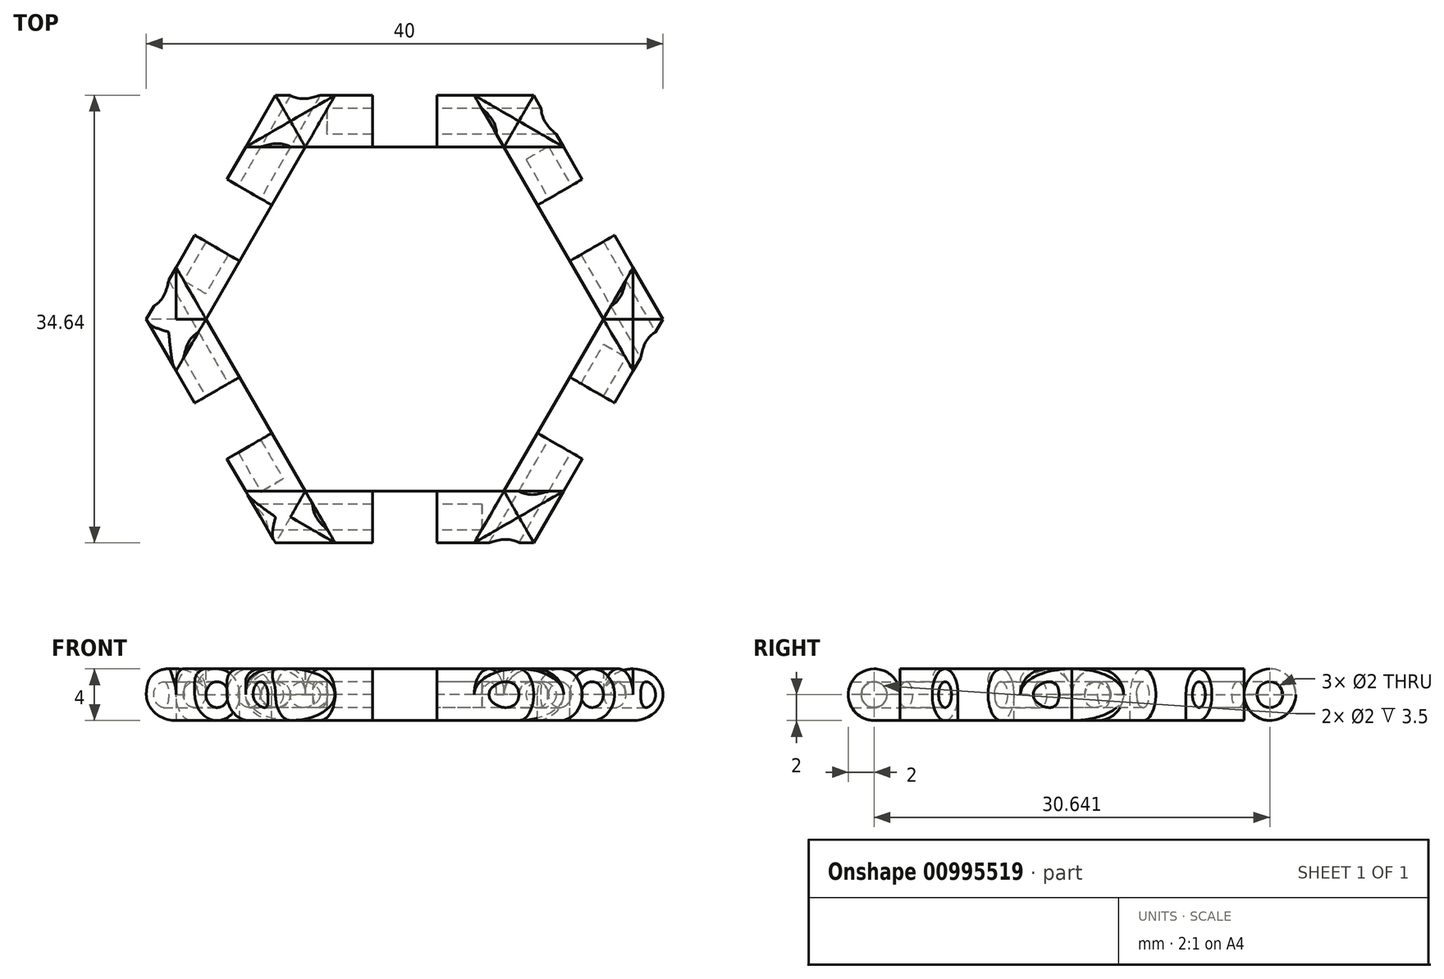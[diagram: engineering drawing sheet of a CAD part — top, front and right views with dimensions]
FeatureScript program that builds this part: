
annotation { "Feature Type Name" : "Feature", "Feature Type Description" : "" }
export const myFeature = defineFeature(function(context is Context, id is Id, definition is map)
    precondition{}
    {
        {
            var Q0;
            Q0=qCreatedBy(makeId("Top.planeOp"),FACE);
            var sketch = newSketch(context, id + "F0", { "sketchPlane" : qUnion([Q0])});
            skPoint(sketch, "E0.center", {"position": v(0, 0) * mm});
            skLineSegment(sketch, "E1", {"start": v(-10, -17.32) * mm, "end": v(10, -17.32) * mm});
            skLineSegment(sketch, "E2", {"start": v(10, -17.32) * mm, "end": v(20, 0) * mm});
            skLineSegment(sketch, "E3", {"start": v(20, 0) * mm, "end": v(10, 17.32) * mm});
            skLineSegment(sketch, "E4", {"start": v(10, 17.32) * mm, "end": v(-10, 17.32) * mm});
            skLineSegment(sketch, "E5", {"start": v(-10, 17.32) * mm, "end": v(-20, 0) * mm});
            skLineSegment(sketch, "E6", {"start": v(-20, 0) * mm, "end": v(-10, -17.32) * mm});
            skSolve(sketch);
        }
        {
            var Q0;
            Q0=makeQuery(id+"F0.imprint","IMPRINT",FACE,{"disambiguationData":[TD([[makeQuery(id+"F0.imprint","IMPRINT",EDGE,{"derivedFrom":sQuery(id+"F0.wireOp",EDGE,"E1")}),1.0]])]});
            extrude(context, id + "F1", {"entities" : qUnion([Q0]), "depth" : 4 * mm, "offsetDistance" : 25 * mm});
        }
        {
            var Q0;
            Q0=makeQuery(id+"F1.opExtrude","CAP_FACE",FACE,{"disambiguationData":[OSD([sQuery(id+"F0.wireOp",EDGE,"E1"),sQuery(id+"F0.wireOp",EDGE,"E2"),sQuery(id+"F0.wireOp",EDGE,"E3"),sQuery(id+"F0.wireOp",EDGE,"E4"),sQuery(id+"F0.wireOp",EDGE,"E5"),sQuery(id+"F0.wireOp",EDGE,"E6")])],"isStart":false});
            var sketch = newSketch(context, id + "F2", { "sketchPlane" : qUnion([Q0])});
            skLineSegment(sketch, "E7", {"start": v(-10, -17.32) * mm, "end": v(-13.75, -10.83) * mm});
            skLineSegment(sketch, "E8", {"start": v(-13.75, -10.83) * mm, "end": v(-10.29, -8.83) * mm});
            skLineSegment(sketch, "E9", {"start": v(-10.29, -8.83) * mm, "end": v(-12.79, -4.5) * mm});
            skLineSegment(sketch, "E10", {"start": v(-12.79, -4.5) * mm, "end": v(-16.25, -6.5) * mm});
            skLineSegment(sketch, "E11", {"start": v(-16.25, -6.5) * mm, "end": v(-20, 0) * mm});
            skLineSegment(sketch, "E12.1.0", {"start": v(2.5, -17.32) * mm, "end": v(2.5, -13.32) * mm});
            skLineSegment(sketch, "E12.1.1", {"start": v(2.5, -13.32) * mm, "end": v(-2.5, -13.32) * mm});
            skLineSegment(sketch, "E12.1.2", {"start": v(-2.5, -13.32) * mm, "end": v(-2.5, -17.32) * mm});
            skLineSegment(sketch, "E12.2.0", {"start": v(16.25, -6.5) * mm, "end": v(12.79, -4.5) * mm});
            skLineSegment(sketch, "E12.2.1", {"start": v(12.79, -4.5) * mm, "end": v(10.29, -8.83) * mm});
            skLineSegment(sketch, "E12.2.2", {"start": v(10.29, -8.83) * mm, "end": v(13.75, -10.83) * mm});
            skLineSegment(sketch, "E12.3.0", {"start": v(13.75, 10.83) * mm, "end": v(10.29, 8.83) * mm});
            skLineSegment(sketch, "E12.3.1", {"start": v(10.29, 8.83) * mm, "end": v(12.79, 4.5) * mm});
            skLineSegment(sketch, "E12.3.2", {"start": v(12.79, 4.5) * mm, "end": v(16.25, 6.5) * mm});
            skLineSegment(sketch, "E12.4.0", {"start": v(-2.5, 17.32) * mm, "end": v(-2.5, 13.32) * mm});
            skLineSegment(sketch, "E12.4.1", {"start": v(-2.5, 13.32) * mm, "end": v(2.5, 13.32) * mm});
            skLineSegment(sketch, "E12.4.2", {"start": v(2.5, 13.32) * mm, "end": v(2.5, 17.32) * mm});
            skLineSegment(sketch, "E12.5.0", {"start": v(-16.25, 6.5) * mm, "end": v(-12.79, 4.5) * mm});
            skLineSegment(sketch, "E12.5.1", {"start": v(-12.79, 4.5) * mm, "end": v(-10.29, 8.83) * mm});
            skLineSegment(sketch, "E12.5.2", {"start": v(-10.29, 8.83) * mm, "end": v(-13.75, 10.83) * mm});
            skPoint(sketch, "E12.center", {"position": v(0, 0) * mm});
            skSolve(sketch);
        }
        {
            var Q0;
            {var subQ0=sQuery(id+"F2.wireOp",EDGE,"E12.4.0");Q0=makeQuery(id+"F2.imprint","IMPRINT",FACE,{"disambiguationData":[TD([[makeQuery(id+"F2.imprint","IMPRINT",EDGE,{"derivedFrom":subQ0}),1.0]])]});}
            var Q1;
            {var subQ0=sQuery(id+"F2.wireOp",EDGE,"E12.3.0");Q1=makeQuery(id+"F2.imprint","IMPRINT",FACE,{"disambiguationData":[TD([[makeQuery(id+"F2.imprint","IMPRINT",EDGE,{"derivedFrom":subQ0}),1.0]])]});}
            var Q2;
            {var subQ0=sQuery(id+"F2.wireOp",EDGE,"E12.2.0");Q2=makeQuery(id+"F2.imprint","IMPRINT",FACE,{"disambiguationData":[TD([[makeQuery(id+"F2.imprint","IMPRINT",EDGE,{"derivedFrom":subQ0}),1.0]])]});}
            var Q3;
            {var subQ0=sQuery(id+"F2.wireOp",EDGE,"E12.1.0");Q3=makeQuery(id+"F2.imprint","IMPRINT",FACE,{"disambiguationData":[TD([[makeQuery(id+"F2.imprint","IMPRINT",EDGE,{"derivedFrom":subQ0}),1.0]])]});}
            var Q4;
            {var subQ0=sQuery(id+"F2.wireOp",EDGE,"E8");Q4=makeQuery(id+"F2.imprint","IMPRINT",FACE,{"disambiguationData":[TD([[makeQuery(id+"F2.imprint","IMPRINT",EDGE,{"derivedFrom":subQ0}),1.0]])]});}
            var Q5;
            {var subQ0=sQuery(id+"F2.wireOp",EDGE,"E12.5.0");Q5=makeQuery(id+"F2.imprint","IMPRINT",FACE,{"disambiguationData":[TD([[makeQuery(id+"F2.imprint","IMPRINT",EDGE,{"derivedFrom":subQ0}),1.0]])]});}
            extrude(context, id + "F3", {"entities" : qUnion([Q0, Q1, Q2, Q3, Q4, Q5]), "operationType" : NewBodyOperationType.REMOVE, "oppositeDirection" : true, "depth" : 25 * mm, "offsetDistance" : 25 * mm});
        }
        {
            var Q0;
            Q0=makeQuery(id+"F3.boolean.opBoolean","COPY",FACE,{"derivedFrom":makeQuery(id+"F3.opExtrude","SWEPT_FACE",FACE,{"disambiguationData":[OSD([sQuery(id+"F2.wireOp",EDGE,"E12.3.0")])]})});
            var sketch = newSketch(context, id + "F4", { "sketchPlane" : qUnion([Q0])});
            skLineSegment(sketch, "E13", {"start": v(17.32, 0) * mm, "end": v(16.32, 0) * mm});
            skLineSegment(sketch, "E14", {"start": v(16.32, 0) * mm, "end": v(15.32, 0) * mm});
            skLineSegment(sketch, "E15", {"start": v(15.32, 0) * mm, "end": v(15.32, 2) * mm});
            skCircle(sketch, "E16", {"center": v(15.32, 2) * mm, "radius": 1 * mm});
            skCircle(sketch, "E17", {"center": v(15.32, 2) * mm, "radius": 2 * mm});
            skSolve(sketch);
        }
        {
            var Q0;
            Q0=makeQuery(id+"F4.imprint","IMPRINT",FACE,{"disambiguationData":[TD([[makeQuery(id+"F4.imprint","IMPRINT",EDGE,{"derivedFrom":sQuery(id+"F4.wireOp",EDGE,"E16")}),1.0]])]});
            extrude(context, id + "F5", {"entities" : qUnion([Q0]), "operationType" : NewBodyOperationType.REMOVE, "oppositeDirection" : true, "depth" : 3.5 * mm, "offsetDistance" : 25 * mm, "hasSecondDirection" : true, "secondDirectionOppositeDirection" : false, "secondDirectionDepth" : 25 * mm});
        }
        {
            var Q0;
            Q0=makeQuery(id+"F3.boolean.opBoolean","COPY",FACE,{"derivedFrom":makeQuery(id+"F3.opExtrude","SWEPT_FACE",FACE,{"disambiguationData":[OSD([sQuery(id+"F2.wireOp",EDGE,"E12.2.0")])]})});
            var sketch = newSketch(context, id + "F6", { "sketchPlane" : qUnion([Q0])});
            skLineSegment(sketch, "E18", {"start": v(17.32, 0) * mm, "end": v(16.32, 0) * mm});
            skLineSegment(sketch, "E19", {"start": v(16.32, 0) * mm, "end": v(15.32, 0) * mm});
            skLineSegment(sketch, "E20", {"start": v(15.32, 0) * mm, "end": v(15.32, 2) * mm});
            skCircle(sketch, "E21", {"center": v(15.32, 2) * mm, "radius": 1 * mm});
            skCircle(sketch, "E22", {"center": v(15.32, 2) * mm, "radius": 2 * mm});
            skSolve(sketch);
        }
        {
            var Q0;
            Q0=makeQuery(id+"F6.imprint","IMPRINT",FACE,{"disambiguationData":[TD([[makeQuery(id+"F6.imprint","IMPRINT",EDGE,{"derivedFrom":sQuery(id+"F6.wireOp",EDGE,"E21")}),1.0]])]});
            extrude(context, id + "F7", {"entities" : qUnion([Q0]), "operationType" : NewBodyOperationType.REMOVE, "depth" : 25 * mm, "offsetDistance" : 25 * mm, "hasSecondDirection" : true, "secondDirectionOppositeDirection" : true, "secondDirectionDepth" : 3.5 * mm});
        }
        {
            var Q0;
            Q0=makeQuery(id+"F3.boolean.opBoolean","COPY",FACE,{"derivedFrom":makeQuery(id+"F3.opExtrude","SWEPT_FACE",FACE,{"disambiguationData":[OSD([sQuery(id+"F2.wireOp",EDGE,"E12.1.0")])]})});
            var sketch = newSketch(context, id + "F8", { "sketchPlane" : qUnion([Q0])});
            skLineSegment(sketch, "E23", {"start": v(17.32, 0) * mm, "end": v(15.32, 0) * mm});
            skLineSegment(sketch, "E24", {"start": v(15.32, 0) * mm, "end": v(15.32, 2) * mm});
            skCircle(sketch, "E25", {"center": v(15.32, 2) * mm, "radius": 1 * mm});
            skCircle(sketch, "E26", {"center": v(15.32, 2) * mm, "radius": 2 * mm});
            skSolve(sketch);
        }
        {
            var Q0;
            Q0=makeQuery(id+"F8.imprint","IMPRINT",FACE,{"disambiguationData":[TD([[makeQuery(id+"F8.imprint","IMPRINT",EDGE,{"derivedFrom":sQuery(id+"F8.wireOp",EDGE,"E25")}),1.0]])]});
            extrude(context, id + "F9", {"entities" : qUnion([Q0]), "operationType" : NewBodyOperationType.REMOVE, "oppositeDirection" : true, "depth" : 3.5 * mm, "offsetDistance" : 25 * mm, "hasSecondDirection" : true, "secondDirectionOppositeDirection" : false, "secondDirectionDepth" : 25 * mm});
        }
        {
            var Q0;
            Q0=makeQuery(id+"F3.boolean.opBoolean","COPY",FACE,{"derivedFrom":makeQuery(id+"F3.opExtrude","SWEPT_FACE",FACE,{"disambiguationData":[OSD([sQuery(id+"F2.wireOp",EDGE,"E8")])]})});
            var sketch = newSketch(context, id + "F10", { "sketchPlane" : qUnion([Q0])});
            skLineSegment(sketch, "E27", {"start": v(17.32, 0) * mm, "end": v(15.32, 0) * mm});
            skLineSegment(sketch, "E28", {"start": v(15.32, 0) * mm, "end": v(15.32, 2) * mm});
            skCircle(sketch, "E29", {"center": v(15.32, 2) * mm, "radius": 1 * mm});
            skSolve(sketch);
        }
        {
            var Q0;
            Q0=makeQuery(id+"F10.imprint","IMPRINT",FACE,{"disambiguationData":[TD([[makeQuery(id+"F10.imprint","IMPRINT",EDGE,{"derivedFrom":sQuery(id+"F10.wireOp",EDGE,"E29")}),1.0]])]});
            extrude(context, id + "F11", {"entities" : qUnion([Q0]), "operationType" : NewBodyOperationType.REMOVE, "depth" : 25 * mm, "offsetDistance" : 25 * mm, "hasSecondDirection" : true, "secondDirectionOppositeDirection" : true, "secondDirectionDepth" : 3.5 * mm});
        }
        {
            var Q0;
            Q0=makeQuery(id+"F3.boolean.opBoolean","COPY",FACE,{"derivedFrom":makeQuery(id+"F3.opExtrude","SWEPT_FACE",FACE,{"disambiguationData":[OSD([sQuery(id+"F2.wireOp",EDGE,"E12.5.0")])]})});
            var sketch = newSketch(context, id + "F12", { "sketchPlane" : qUnion([Q0])});
            skLineSegment(sketch, "E30", {"start": v(17.32, 0) * mm, "end": v(15.32, 0) * mm});
            skLineSegment(sketch, "E31", {"start": v(15.32, 0) * mm, "end": v(15.32, 2) * mm});
            skCircle(sketch, "E32", {"center": v(15.32, 2) * mm, "radius": 1 * mm});
            skCircle(sketch, "E33", {"center": v(15.32, 2) * mm, "radius": 2 * mm});
            skSolve(sketch);
        }
        {
            var Q0;
            Q0=makeQuery(id+"F12.imprint","IMPRINT",FACE,{"disambiguationData":[TD([[makeQuery(id+"F12.imprint","IMPRINT",EDGE,{"derivedFrom":sQuery(id+"F12.wireOp",EDGE,"E32")}),1.0]])]});
            extrude(context, id + "F13", {"entities" : qUnion([Q0]), "operationType" : NewBodyOperationType.REMOVE, "depth" : 25 * mm, "offsetDistance" : 25 * mm, "hasSecondDirection" : true, "secondDirectionOppositeDirection" : true, "secondDirectionDepth" : 3.5 * mm});
        }
        {
            var Q0;
            Q0=makeQuery(id+"F3.boolean.opBoolean","COPY",FACE,{"derivedFrom":makeQuery(id+"F3.opExtrude","SWEPT_FACE",FACE,{"disambiguationData":[OSD([sQuery(id+"F2.wireOp",EDGE,"E12.4.0")])]})});
            var sketch = newSketch(context, id + "F14", { "sketchPlane" : qUnion([Q0])});
            skLineSegment(sketch, "E34", {"start": v(17.32, 4) * mm, "end": v(15.32, 4) * mm});
            skLineSegment(sketch, "E35", {"start": v(15.32, 4) * mm, "end": v(15.32, 2) * mm});
            skCircle(sketch, "E36", {"center": v(15.32, 2) * mm, "radius": 1 * mm});
            skCircle(sketch, "E37", {"center": v(15.32, 2) * mm, "radius": 2 * mm});
            skSolve(sketch);
        }
        {
            var Q0;
            Q0=makeQuery(id+"F14.imprint","IMPRINT",FACE,{"disambiguationData":[TD([[makeQuery(id+"F14.imprint","IMPRINT",EDGE,{"derivedFrom":sQuery(id+"F14.wireOp",EDGE,"E36")}),1.0]])]});
            extrude(context, id + "F15", {"entities" : qUnion([Q0]), "operationType" : NewBodyOperationType.REMOVE, "depth" : 25 * mm, "offsetDistance" : 25 * mm, "hasSecondDirection" : true, "secondDirectionOppositeDirection" : true, "secondDirectionDepth" : 3.5 * mm});
        }
        {
            var Q0;
            {var subQ0=sQuery(id+"F0.wireOp",EDGE,"E1");var subQ1=sQuery(id+"F0.wireOp",EDGE,"E6");Q0=makeQuery(id+"F3.boolean.opBoolean","SPLIT",EDGE,{"disambiguationData":[TD([makeQuery(id+"F1.opExtrude","SWEPT_FACE",FACE,{"disambiguationData":[OSD([subQ1])]})])],"derivedFrom":makeQuery(id+"F1.opExtrude","CAP_EDGE",EDGE,{"disambiguationData":[OSD([subQ0])],"isStart":false})});}
            var Q1;
            {var subQ0=sQuery(id+"F0.wireOp",EDGE,"E1");var subQ1=sQuery(id+"F0.wireOp",EDGE,"E6");Q1=makeQuery(id+"F3.boolean.opBoolean","SPLIT",EDGE,{"disambiguationData":[TD([makeQuery(id+"F1.opExtrude","SWEPT_FACE",FACE,{"disambiguationData":[OSD([subQ1])]})])],"derivedFrom":makeQuery(id+"F1.opExtrude","CAP_EDGE",EDGE,{"disambiguationData":[OSD([subQ0])],"isStart":true})});}
            var Q2;
            {var subQ0=sQuery(id+"F0.wireOp",EDGE,"E1");var subQ1=sQuery(id+"F0.wireOp",EDGE,"E2");Q2=makeQuery(id+"F3.boolean.opBoolean","SPLIT",EDGE,{"disambiguationData":[TD([makeQuery(id+"F1.opExtrude","SWEPT_FACE",FACE,{"disambiguationData":[OSD([subQ1])]})])],"derivedFrom":makeQuery(id+"F1.opExtrude","CAP_EDGE",EDGE,{"disambiguationData":[OSD([subQ0])],"isStart":false})});}
            var Q3;
            {var subQ0=sQuery(id+"F0.wireOp",EDGE,"E1");var subQ1=sQuery(id+"F0.wireOp",EDGE,"E2");Q3=makeQuery(id+"F3.boolean.opBoolean","SPLIT",EDGE,{"disambiguationData":[TD([makeQuery(id+"F1.opExtrude","SWEPT_FACE",FACE,{"disambiguationData":[OSD([subQ1])]})])],"derivedFrom":makeQuery(id+"F1.opExtrude","CAP_EDGE",EDGE,{"disambiguationData":[OSD([subQ0])],"isStart":true})});}
            var Q4;
            {var subQ0=sQuery(id+"F0.wireOp",EDGE,"E1");var subQ1=sQuery(id+"F0.wireOp",EDGE,"E2");Q4=makeQuery(id+"F3.boolean.opBoolean","SPLIT",EDGE,{"disambiguationData":[TD([makeQuery(id+"F1.opExtrude","SWEPT_FACE",FACE,{"disambiguationData":[OSD([subQ0])]})])],"derivedFrom":makeQuery(id+"F1.opExtrude","CAP_EDGE",EDGE,{"disambiguationData":[OSD([subQ1])],"isStart":false})});}
            var Q5;
            {var subQ0=sQuery(id+"F0.wireOp",EDGE,"E1");var subQ1=sQuery(id+"F0.wireOp",EDGE,"E2");Q5=makeQuery(id+"F3.boolean.opBoolean","SPLIT",EDGE,{"disambiguationData":[TD([makeQuery(id+"F1.opExtrude","SWEPT_FACE",FACE,{"disambiguationData":[OSD([subQ0])]})])],"derivedFrom":makeQuery(id+"F1.opExtrude","CAP_EDGE",EDGE,{"disambiguationData":[OSD([subQ1])],"isStart":true})});}
            var Q6;
            {var subQ0=sQuery(id+"F0.wireOp",EDGE,"E3");var subQ1=sQuery(id+"F0.wireOp",EDGE,"E2");Q6=makeQuery(id+"F3.boolean.opBoolean","SPLIT",EDGE,{"disambiguationData":[TD([makeQuery(id+"F1.opExtrude","SWEPT_FACE",FACE,{"disambiguationData":[OSD([subQ0])]})])],"derivedFrom":makeQuery(id+"F1.opExtrude","CAP_EDGE",EDGE,{"disambiguationData":[OSD([subQ1])],"isStart":false})});}
            var Q7;
            {var subQ0=sQuery(id+"F0.wireOp",EDGE,"E3");var subQ1=sQuery(id+"F0.wireOp",EDGE,"E2");Q7=makeQuery(id+"F3.boolean.opBoolean","SPLIT",EDGE,{"disambiguationData":[TD([makeQuery(id+"F1.opExtrude","SWEPT_FACE",FACE,{"disambiguationData":[OSD([subQ0])]})])],"derivedFrom":makeQuery(id+"F1.opExtrude","CAP_EDGE",EDGE,{"disambiguationData":[OSD([subQ1])],"isStart":true})});}
            var Q8;
            {var subQ0=sQuery(id+"F0.wireOp",EDGE,"E3");var subQ1=sQuery(id+"F0.wireOp",EDGE,"E2");Q8=makeQuery(id+"F3.boolean.opBoolean","SPLIT",EDGE,{"disambiguationData":[TD([makeQuery(id+"F1.opExtrude","SWEPT_FACE",FACE,{"disambiguationData":[OSD([subQ1])]})])],"derivedFrom":makeQuery(id+"F1.opExtrude","CAP_EDGE",EDGE,{"disambiguationData":[OSD([subQ0])],"isStart":false})});}
            var Q9;
            {var subQ0=sQuery(id+"F0.wireOp",EDGE,"E3");var subQ1=sQuery(id+"F0.wireOp",EDGE,"E2");Q9=makeQuery(id+"F3.boolean.opBoolean","SPLIT",EDGE,{"disambiguationData":[TD([makeQuery(id+"F1.opExtrude","SWEPT_FACE",FACE,{"disambiguationData":[OSD([subQ1])]})])],"derivedFrom":makeQuery(id+"F1.opExtrude","CAP_EDGE",EDGE,{"disambiguationData":[OSD([subQ0])],"isStart":true})});}
            var Q10;
            {var subQ0=sQuery(id+"F0.wireOp",EDGE,"E4");var subQ1=sQuery(id+"F0.wireOp",EDGE,"E3");Q10=makeQuery(id+"F3.boolean.opBoolean","SPLIT",EDGE,{"disambiguationData":[TD([makeQuery(id+"F1.opExtrude","SWEPT_FACE",FACE,{"disambiguationData":[OSD([subQ0])]})])],"derivedFrom":makeQuery(id+"F1.opExtrude","CAP_EDGE",EDGE,{"disambiguationData":[OSD([subQ1])],"isStart":false})});}
            var Q11;
            {var subQ0=sQuery(id+"F0.wireOp",EDGE,"E4");var subQ1=sQuery(id+"F0.wireOp",EDGE,"E3");Q11=makeQuery(id+"F3.boolean.opBoolean","SPLIT",EDGE,{"disambiguationData":[TD([makeQuery(id+"F1.opExtrude","SWEPT_FACE",FACE,{"disambiguationData":[OSD([subQ0])]})])],"derivedFrom":makeQuery(id+"F1.opExtrude","CAP_EDGE",EDGE,{"disambiguationData":[OSD([subQ1])],"isStart":true})});}
            var Q12;
            {var subQ0=sQuery(id+"F0.wireOp",EDGE,"E4");var subQ1=sQuery(id+"F0.wireOp",EDGE,"E3");Q12=makeQuery(id+"F3.boolean.opBoolean","SPLIT",EDGE,{"disambiguationData":[TD([makeQuery(id+"F1.opExtrude","SWEPT_FACE",FACE,{"disambiguationData":[OSD([subQ1])]})])],"derivedFrom":makeQuery(id+"F1.opExtrude","CAP_EDGE",EDGE,{"disambiguationData":[OSD([subQ0])],"isStart":false})});}
            var Q13;
            {var subQ0=sQuery(id+"F0.wireOp",EDGE,"E4");var subQ1=sQuery(id+"F0.wireOp",EDGE,"E3");Q13=makeQuery(id+"F3.boolean.opBoolean","SPLIT",EDGE,{"disambiguationData":[TD([makeQuery(id+"F1.opExtrude","SWEPT_FACE",FACE,{"disambiguationData":[OSD([subQ1])]})])],"derivedFrom":makeQuery(id+"F1.opExtrude","CAP_EDGE",EDGE,{"disambiguationData":[OSD([subQ0])],"isStart":true})});}
            var Q14;
            {var subQ0=sQuery(id+"F0.wireOp",EDGE,"E5");var subQ1=sQuery(id+"F0.wireOp",EDGE,"E4");Q14=makeQuery(id+"F3.boolean.opBoolean","SPLIT",EDGE,{"disambiguationData":[TD([makeQuery(id+"F1.opExtrude","SWEPT_FACE",FACE,{"disambiguationData":[OSD([subQ0])]})])],"derivedFrom":makeQuery(id+"F1.opExtrude","CAP_EDGE",EDGE,{"disambiguationData":[OSD([subQ1])],"isStart":true})});}
            var Q15;
            {var subQ0=sQuery(id+"F0.wireOp",EDGE,"E5");var subQ1=sQuery(id+"F0.wireOp",EDGE,"E4");Q15=makeQuery(id+"F3.boolean.opBoolean","SPLIT",EDGE,{"disambiguationData":[TD([makeQuery(id+"F1.opExtrude","SWEPT_FACE",FACE,{"disambiguationData":[OSD([subQ0])]})])],"derivedFrom":makeQuery(id+"F1.opExtrude","CAP_EDGE",EDGE,{"disambiguationData":[OSD([subQ1])],"isStart":false})});}
            var Q16;
            {var subQ0=sQuery(id+"F0.wireOp",EDGE,"E5");var subQ1=sQuery(id+"F0.wireOp",EDGE,"E4");Q16=makeQuery(id+"F3.boolean.opBoolean","SPLIT",EDGE,{"disambiguationData":[TD([makeQuery(id+"F1.opExtrude","SWEPT_FACE",FACE,{"disambiguationData":[OSD([subQ1])]})])],"derivedFrom":makeQuery(id+"F1.opExtrude","CAP_EDGE",EDGE,{"disambiguationData":[OSD([subQ0])],"isStart":false})});}
            var Q17;
            {var subQ0=sQuery(id+"F0.wireOp",EDGE,"E5");var subQ1=sQuery(id+"F0.wireOp",EDGE,"E4");Q17=makeQuery(id+"F3.boolean.opBoolean","SPLIT",EDGE,{"disambiguationData":[TD([makeQuery(id+"F1.opExtrude","SWEPT_FACE",FACE,{"disambiguationData":[OSD([subQ1])]})])],"derivedFrom":makeQuery(id+"F1.opExtrude","CAP_EDGE",EDGE,{"disambiguationData":[OSD([subQ0])],"isStart":true})});}
            var Q18;
            {var subQ0=sQuery(id+"F0.wireOp",EDGE,"E6");var subQ1=sQuery(id+"F0.wireOp",EDGE,"E5");Q18=makeQuery(id+"F3.boolean.opBoolean","SPLIT",EDGE,{"disambiguationData":[TD([makeQuery(id+"F1.opExtrude","SWEPT_FACE",FACE,{"disambiguationData":[OSD([subQ0])]})])],"derivedFrom":makeQuery(id+"F1.opExtrude","CAP_EDGE",EDGE,{"disambiguationData":[OSD([subQ1])],"isStart":false})});}
            var Q19;
            {var subQ0=sQuery(id+"F0.wireOp",EDGE,"E6");var subQ1=sQuery(id+"F0.wireOp",EDGE,"E5");Q19=makeQuery(id+"F3.boolean.opBoolean","SPLIT",EDGE,{"disambiguationData":[TD([makeQuery(id+"F1.opExtrude","SWEPT_FACE",FACE,{"disambiguationData":[OSD([subQ0])]})])],"derivedFrom":makeQuery(id+"F1.opExtrude","CAP_EDGE",EDGE,{"disambiguationData":[OSD([subQ1])],"isStart":true})});}
            var Q20;
            {var subQ0=sQuery(id+"F0.wireOp",EDGE,"E6");var subQ1=sQuery(id+"F0.wireOp",EDGE,"E5");Q20=makeQuery(id+"F3.boolean.opBoolean","SPLIT",EDGE,{"disambiguationData":[TD([makeQuery(id+"F1.opExtrude","SWEPT_FACE",FACE,{"disambiguationData":[OSD([subQ1])]})])],"derivedFrom":makeQuery(id+"F1.opExtrude","CAP_EDGE",EDGE,{"disambiguationData":[OSD([subQ0])],"isStart":true})});}
            var Q21;
            {var subQ0=sQuery(id+"F0.wireOp",EDGE,"E6");var subQ1=sQuery(id+"F0.wireOp",EDGE,"E5");Q21=makeQuery(id+"F3.boolean.opBoolean","SPLIT",EDGE,{"disambiguationData":[TD([makeQuery(id+"F1.opExtrude","SWEPT_FACE",FACE,{"disambiguationData":[OSD([subQ1])]})])],"derivedFrom":makeQuery(id+"F1.opExtrude","CAP_EDGE",EDGE,{"disambiguationData":[OSD([subQ0])],"isStart":false})});}
            var Q22;
            {var subQ0=sQuery(id+"F0.wireOp",EDGE,"E1");var subQ1=sQuery(id+"F0.wireOp",EDGE,"E6");Q22=makeQuery(id+"F3.boolean.opBoolean","SPLIT",EDGE,{"disambiguationData":[TD([makeQuery(id+"F1.opExtrude","SWEPT_FACE",FACE,{"disambiguationData":[OSD([subQ0])]})])],"derivedFrom":makeQuery(id+"F1.opExtrude","CAP_EDGE",EDGE,{"disambiguationData":[OSD([subQ1])],"isStart":true})});}
            var Q23;
            {var subQ0=sQuery(id+"F0.wireOp",EDGE,"E1");var subQ1=sQuery(id+"F0.wireOp",EDGE,"E6");Q23=makeQuery(id+"F3.boolean.opBoolean","SPLIT",EDGE,{"disambiguationData":[TD([makeQuery(id+"F1.opExtrude","SWEPT_FACE",FACE,{"disambiguationData":[OSD([subQ0])]})])],"derivedFrom":makeQuery(id+"F1.opExtrude","CAP_EDGE",EDGE,{"disambiguationData":[OSD([subQ1])],"isStart":false})});}
            fillet(context, id + "F16", {"entities" : qUnion([Q0, Q1, Q2, Q3, Q4, Q5, Q6, Q7, Q8, Q9, Q10, Q11, Q12, Q13, Q14, Q15, Q16, Q17, Q18, Q19, Q20, Q21, Q22, Q23]), "radius" : 1 * mm, "tangentPropagation" : true, "allowEdgeOverflow" : false});
        }
        {
            var Q0;
            Q0=makeQuery(id+"F3.boolean.opBoolean","COPY",FACE,{"derivedFrom":makeQuery(id+"F3.opExtrude","SWEPT_FACE",FACE,{"disambiguationData":[OSD([sQuery(id+"F2.wireOp",EDGE,"E8")])]})});
            var sketch = newSketch(context, id + "F17", { "sketchPlane" : qUnion([Q0])});
            skCircle(sketch, "E38", {"center": v(15.32, 2) * mm, "radius": 2 * mm});
            skSolve(sketch);
        }
        {
            var Q0;
            {var subQ0=sQuery(id+"F17.wireOp",EDGE,"E38");var subQ1=sQuery(id+"F2.wireOp",EDGE,"E8");var subQ2=makeQuery(id+"F3.boolean.opBoolean","COPY",EDGE,{"derivedFrom":makeQuery(id+"F3.opExtrude","CAP_EDGE",EDGE,{"disambiguationData":[OSD([subQ1])],"isStart":true})});var subQ3=makeQuery(id+"F17.imprint","INTERSECT",VERTEX,{"derivedFrom":[subQ2,subQ0]});Q0=makeQuery(id+"F17.imprint","IMPRINT",FACE,{"disambiguationData":[TD([[makeQuery(id+"F17.imprint","IMPRINT",EDGE,{"disambiguationData":[TD([[subQ3,1.0]])],"derivedFrom":subQ0}),-1.0]])]});}
            var Q1;
            {var subQ1=sQuery(id+"F2.wireOp",EDGE,"E8");var subQ2=sQuery(id+"F0.wireOp",EDGE,"E6");var subQ5=makeQuery(id+"F3.opExtrude","SWEPT_FACE",FACE,{"disambiguationData":[OSD([subQ1])]});var subQ6=sQuery(id+"F0.wireOp",EDGE,"E1");var subQ10=makeQuery(id+"F16.opFillet","BLEND_EDGE",EDGE,{"blendedFrom":[makeQuery(id+"F3.boolean.opBoolean","SPLIT",EDGE,{"disambiguationData":[TD([makeQuery(id+"F1.opExtrude","SWEPT_FACE",FACE,{"disambiguationData":[OSD([subQ6])]})])],"derivedFrom":makeQuery(id+"F1.opExtrude","CAP_EDGE",EDGE,{"disambiguationData":[OSD([subQ2])],"isStart":true})}),makeQuery(id+"F3.boolean.opBoolean","COPY",FACE,{"derivedFrom":subQ5})],"blendedInto":[makeQuery(id+"F3.boolean.opBoolean","COPY",FACE,{"derivedFrom":subQ5})]});Q1=makeQuery(id+"F17.imprint","IMPRINT",FACE,{"disambiguationData":[TD([[makeQuery(id+"F17.imprint","IMPRINT",EDGE,{"derivedFrom":subQ10}),1.0]])]});}
            extrude(context, id + "F18", {"entities" : qUnion([Q0, Q1]), "operationType" : NewBodyOperationType.REMOVE, "oppositeDirection" : true, "depth" : 25 * mm, "offsetDistance" : 25 * mm, "hasSecondDirection" : true, "secondDirectionOppositeDirection" : false, "secondDirectionDepth" : 25 * mm});
        }
        {
            var Q0;
            {var subQ0=sQuery(id+"F12.wireOp",EDGE,"E33");var subQ1=sQuery(id+"F2.wireOp",EDGE,"E12.5.0");var subQ2=makeQuery(id+"F3.boolean.opBoolean","COPY",EDGE,{"derivedFrom":makeQuery(id+"F3.opExtrude","CAP_EDGE",EDGE,{"disambiguationData":[OSD([subQ1])],"isStart":true})});var subQ3=makeQuery(id+"F12.imprint","INTERSECT",VERTEX,{"derivedFrom":[subQ2,subQ0]});Q0=makeQuery(id+"F12.imprint","IMPRINT",FACE,{"disambiguationData":[TD([[makeQuery(id+"F12.imprint","IMPRINT",EDGE,{"disambiguationData":[TD([[subQ3,1.0]])],"derivedFrom":subQ0}),-1.0]])]});}
            var Q1;
            {var subQ0=sQuery(id+"F12.wireOp",EDGE,"E30");Q1=makeQuery(id+"F12.imprint","IMPRINT",FACE,{"disambiguationData":[TD([[makeQuery(id+"F12.imprint","IMPRINT",EDGE,{"derivedFrom":subQ0}),-1.0]])]});}
            extrude(context, id + "F19", {"entities" : qUnion([Q0, Q1]), "operationType" : NewBodyOperationType.REMOVE, "oppositeDirection" : true, "depth" : 25 * mm, "offsetDistance" : 25 * mm, "hasSecondDirection" : true, "secondDirectionOppositeDirection" : false, "secondDirectionDepth" : 25 * mm});
        }
        {
            var Q0;
            {var subQ0=sQuery(id+"F14.wireOp",EDGE,"E34");Q0=makeQuery(id+"F14.imprint","IMPRINT",FACE,{"disambiguationData":[TD([[makeQuery(id+"F14.imprint","IMPRINT",EDGE,{"derivedFrom":subQ0}),1.0]])]});}
            var Q1;
            {var subQ0=sQuery(id+"F14.wireOp",EDGE,"E37");var subQ1=sQuery(id+"F2.wireOp",EDGE,"E12.4.0");var subQ2=sQuery(id+"F0.wireOp",EDGE,"E4");var subQ3=makeQuery(id+"F3.boolean.opBoolean","COPY",EDGE,{"derivedFrom":makeQuery(id+"F3.opExtrude","SWEPT_EDGE",EDGE,{"disambiguationData":[OSD([subQ2,subQ1])]})});var subQ4=makeQuery(id+"F14.imprint","INTERSECT",VERTEX,{"derivedFrom":[subQ3,subQ0]});Q1=makeQuery(id+"F14.imprint","IMPRINT",FACE,{"disambiguationData":[TD([[makeQuery(id+"F14.imprint","IMPRINT",EDGE,{"disambiguationData":[TD([[subQ4,1.0]])],"derivedFrom":subQ0}),-1.0]])]});}
            extrude(context, id + "F20", {"entities" : qUnion([Q0, Q1]), "operationType" : NewBodyOperationType.REMOVE, "oppositeDirection" : true, "depth" : 25 * mm, "offsetDistance" : 25 * mm, "hasSecondDirection" : true, "secondDirectionOppositeDirection" : false, "secondDirectionDepth" : 25 * mm});
        }
        {
            var Q0;
            {var subQ0=sQuery(id+"F6.wireOp",EDGE,"E22");var subQ1=sQuery(id+"F2.wireOp",EDGE,"E12.2.0");var subQ2=makeQuery(id+"F3.boolean.opBoolean","COPY",EDGE,{"derivedFrom":makeQuery(id+"F3.opExtrude","CAP_EDGE",EDGE,{"disambiguationData":[OSD([subQ1])],"isStart":true})});var subQ3=makeQuery(id+"F6.imprint","INTERSECT",VERTEX,{"derivedFrom":[subQ2,subQ0]});Q0=makeQuery(id+"F6.imprint","IMPRINT",FACE,{"disambiguationData":[TD([[makeQuery(id+"F6.imprint","IMPRINT",EDGE,{"disambiguationData":[TD([[subQ3,1.0]])],"derivedFrom":subQ0}),-1.0]])]});}
            var Q1;
            {var subQ0=sQuery(id+"F6.wireOp",EDGE,"E18");Q1=makeQuery(id+"F6.imprint","IMPRINT",FACE,{"disambiguationData":[TD([[makeQuery(id+"F6.imprint","IMPRINT",EDGE,{"derivedFrom":subQ0}),-1.0]])]});}
            extrude(context, id + "F21", {"entities" : qUnion([Q0, Q1]), "operationType" : NewBodyOperationType.REMOVE, "oppositeDirection" : true, "depth" : 25 * mm, "offsetDistance" : 25 * mm, "hasSecondDirection" : true, "secondDirectionOppositeDirection" : false, "secondDirectionDepth" : 25 * mm});
        }
        {
            var Q0;
            {var subQ0=sQuery(id+"F8.wireOp",EDGE,"E26");var subQ1=sQuery(id+"F2.wireOp",EDGE,"E12.1.0");var subQ2=makeQuery(id+"F3.boolean.opBoolean","COPY",EDGE,{"derivedFrom":makeQuery(id+"F3.opExtrude","CAP_EDGE",EDGE,{"disambiguationData":[OSD([subQ1])],"isStart":true})});var subQ3=makeQuery(id+"F8.imprint","INTERSECT",VERTEX,{"derivedFrom":[subQ2,subQ0]});Q0=makeQuery(id+"F8.imprint","IMPRINT",FACE,{"disambiguationData":[TD([[makeQuery(id+"F8.imprint","IMPRINT",EDGE,{"disambiguationData":[TD([[subQ3,1.0]])],"derivedFrom":subQ0}),-1.0]])]});}
            var Q1;
            {var subQ0=sQuery(id+"F8.wireOp",EDGE,"E23");Q1=makeQuery(id+"F8.imprint","IMPRINT",FACE,{"disambiguationData":[TD([[makeQuery(id+"F8.imprint","IMPRINT",EDGE,{"derivedFrom":subQ0}),-1.0]])]});}
            extrude(context, id + "F22", {"entities" : qUnion([Q0, Q1]), "operationType" : NewBodyOperationType.REMOVE, "oppositeDirection" : true, "depth" : 25 * mm, "offsetDistance" : 25 * mm, "hasSecondDirection" : true, "secondDirectionOppositeDirection" : false, "secondDirectionDepth" : 25 * mm});
        }
        {
            var Q0;
            {var subQ0=sQuery(id+"F4.wireOp",EDGE,"E17");var subQ1=sQuery(id+"F2.wireOp",EDGE,"E12.3.0");var subQ2=makeQuery(id+"F3.boolean.opBoolean","COPY",EDGE,{"derivedFrom":makeQuery(id+"F3.opExtrude","CAP_EDGE",EDGE,{"disambiguationData":[OSD([subQ1])],"isStart":true})});var subQ3=makeQuery(id+"F4.imprint","INTERSECT",VERTEX,{"derivedFrom":[subQ2,subQ0]});Q0=makeQuery(id+"F4.imprint","IMPRINT",FACE,{"disambiguationData":[TD([[makeQuery(id+"F4.imprint","IMPRINT",EDGE,{"disambiguationData":[TD([[subQ3,1.0]])],"derivedFrom":subQ0}),-1.0]])]});}
            var Q1;
            {var subQ0=sQuery(id+"F4.wireOp",EDGE,"E13");Q1=makeQuery(id+"F4.imprint","IMPRINT",FACE,{"disambiguationData":[TD([[makeQuery(id+"F4.imprint","IMPRINT",EDGE,{"derivedFrom":subQ0}),-1.0]])]});}
            extrude(context, id + "F23", {"entities" : qUnion([Q0, Q1]), "operationType" : NewBodyOperationType.REMOVE, "oppositeDirection" : true, "depth" : 25 * mm, "offsetDistance" : 25 * mm, "hasSecondDirection" : true, "secondDirectionOppositeDirection" : false, "secondDirectionDepth" : 25 * mm});
        }
    });
